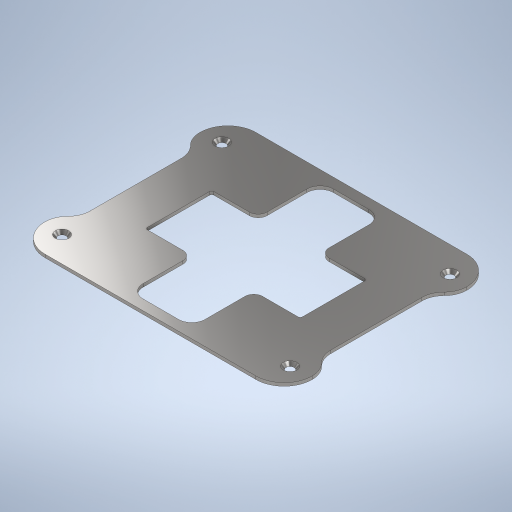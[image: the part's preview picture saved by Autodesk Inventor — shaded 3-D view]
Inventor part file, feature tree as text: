
AUTODESK INVENTOR PART (.ipt)
format: ipt  version: 2023 (Build 270158000, 158)  size: 359,936 bytes
history: native  units: in
note: dims shown in document units (in); Inventor stores cm internally (conversion verified against a paired STEP export)
features: extrude x4, sketch x4, hole x1, fillet x1
ambient origin geometry x8: Origin, YZ Plane, XZ Plane, XY Plane, X Axis, Y Axis, Z Axis, Center Point
bodies: Solid1 (feature_tree)
feature tree (10):
  extrude  "Extrusion1"  Depth=1.875in
  hole  "Hole1"  [1 undecoded]
  extrude  "Extrusion2"  Depth=0.5906in
  extrude  "Extrusion3"  Depth=0.0787in
  extrude  "Extrusion4"  Depth=0.2in
  fillet  "Fillet1"  [1 undecoded]
  sketch  "Sketch1"  dims[d0=1.875in d1=2.375in]
  sketch  "Sketch2"  dims[d2=0.25in d3=0.0276in d4=0.0in]
  sketch  "Sketch5"  dims[d9=0.07in d10=0.146in d11=0.119in d12=0.25in d13=0.5635in d14=1.0in d15=0.8108in d18=0.5906in]
  sketch  "Sketch7"  dims[d19=0.0in d20=0.0in d21=0.1969in d41=0.2in d42=45.0deg d43=0.2in d44=45.0deg d45=0.2in d46=45.0deg d47=0.2in d48=45.0deg d49=1.0in d50=0.0in d51=0.2in d52=45.0deg d53=0.2in d54=45.0deg d57=0.2in d58=45.0deg d59=0.2in d60=45.0deg d72=1.1811in d73=0.5906in d76=2.0276in d77=1.4213in d78=0.7106in d79=1.0138in d80=0.5512in d81=1.6929in d82=0.1181in d83=0.0in d84=0.0in d85=0.0197in d87=0.0787in]
note: 2 required parameter values undecoded (feature->parameter linkage not recoverable at this tier; creation-order binding heuristic only, values carry confidence <= 0.55)
